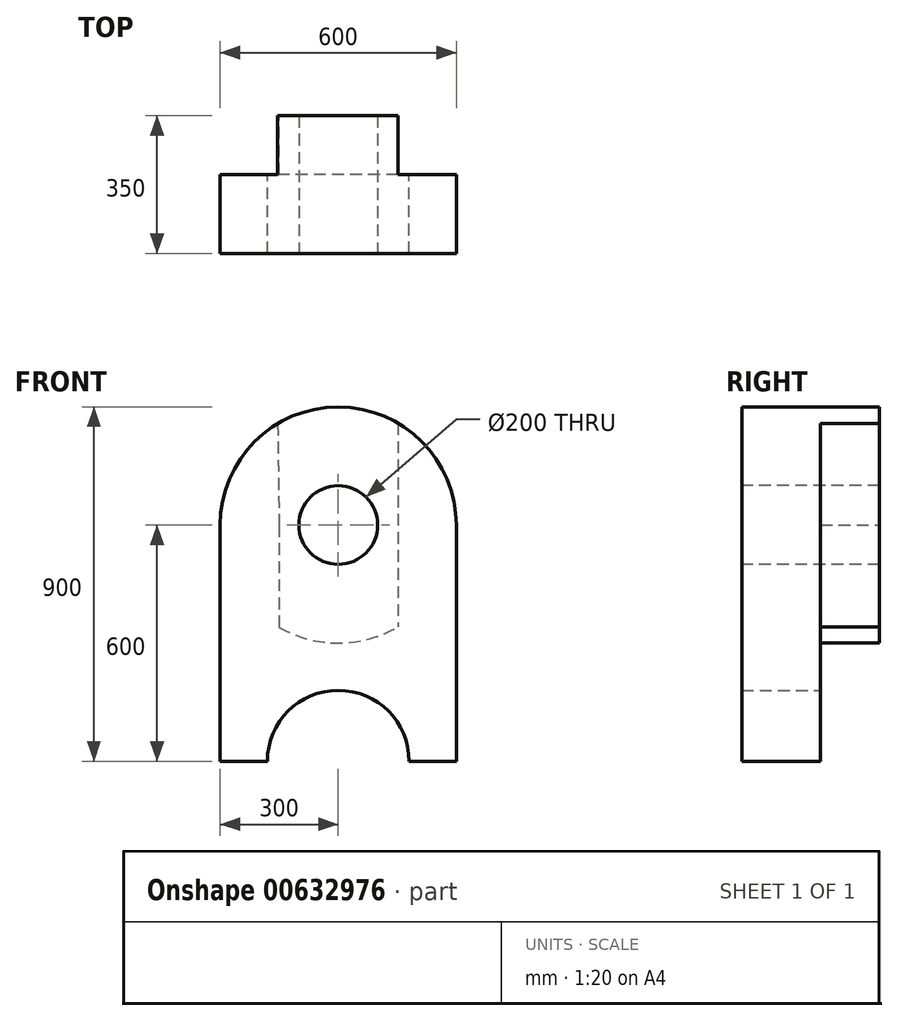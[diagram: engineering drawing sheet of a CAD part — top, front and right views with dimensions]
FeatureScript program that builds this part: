
annotation { "Feature Type Name" : "Feature", "Feature Type Description" : "" }
export const myFeature = defineFeature(function(context is Context, id is Id, definition is map)
    precondition{}
    {
        {
            var Q0;
            Q0=qCreatedBy(makeId("Front.planeOp"),FACE);
            var sketch = newSketch(context, id + "F0", { "sketchPlane" : qUnion([Q0])});
            skLineSegment(sketch, "E0.bottom", {"start": v(300, 300) * mm, "end": v(-300, 300) * mm});
            skLineSegment(sketch, "E0.top", {"start": v(300, -300) * mm, "end": v(-300, -300) * mm});
            skLineSegment(sketch, "E0.left", {"start": v(300, 300) * mm, "end": v(300, -300) * mm});
            skLineSegment(sketch, "E0.right", {"start": v(-300, 300) * mm, "end": v(-300, -300) * mm});
            skPoint(sketch, "E0.middle", {"position": v(0, 0) * mm});
            skArc(sketch, "E1", {"start": v(300, 300) * mm, "mid": v(0, 600) * mm, "end": v(-300, 300) * mm});
            skArc(sketch, "E2", {"start": v(180, -300) * mm, "mid": v(0, -120) * mm, "end": v(-180, -300) * mm});
            skSolve(sketch);
        }
        {
            var Q0;
            {var subQ0=sQuery(id+"F0.wireOp",EDGE,"E2");Q0=makeQuery(id+"F0.imprint","IMPRINT",FACE,{"disambiguationData":[TD([[makeQuery(id+"F0.imprint","IMPRINT",EDGE,{"derivedFrom":subQ0}),1.0]])]});}
            var sketch = newSketch(context, id + "F1", { "sketchPlane" : qUnion([Q0])});
            skSolve(sketch);
        }
        {
            var Q0;
            Q0=makeQuery(id+"F0.imprint","IMPRINT",FACE,{"disambiguationData":[TD([[makeQuery(id+"F0.imprint","IMPRINT",EDGE,{"derivedFrom":sQuery(id+"F0.wireOp",EDGE,"E0.bottom")}),1.0]])]});
            var Q1;
            Q1=makeQuery(id+"F0.imprint","IMPRINT",FACE,{"disambiguationData":[TD([[makeQuery(id+"F0.imprint","IMPRINT",EDGE,{"derivedFrom":sQuery(id+"F0.wireOp",EDGE,"E0.bottom")}),-1.0]])]});
            extrude(context, id + "F2", {"entities" : qUnion([Q0, Q1]), "depth" : 350 * mm, "offsetDistance" : 25 * mm});
        }
        {
            var Q0;
            {var subQ0=sQuery(id+"F0.wireOp",EDGE,"E2");Q0=makeQuery(id+"F1.imprint","IMPRINT",FACE,{"disambiguationData":[TD([[makeQuery(id+"F1.imprint","IMPRINT",EDGE,{"derivedFrom":makeQuery(id+"F0.imprint","IMPRINT",EDGE,{"derivedFrom":subQ0})}),1.0]])]});}
            extrude(context, id + "F3", {"entities" : qUnion([Q0]), "operationType" : NewBodyOperationType.REMOVE, "oppositeDirection" : true, "depth" : 25 * mm, "offsetDistance" : 25 * mm});
        }
        {
            var Q0;
            Q0=makeQuery(id+"F2.opExtrude","CAP_FACE",FACE,{"disambiguationData":[OSD([sQuery(id+"F0.wireOp",EDGE,"E0.top"),sQuery(id+"F0.wireOp",EDGE,"E0.left"),sQuery(id+"F0.wireOp",EDGE,"E0.right"),sQuery(id+"F0.wireOp",EDGE,"E1"),sQuery(id+"F0.wireOp",EDGE,"E2")])],"isStart":false});
            var sketch = newSketch(context, id + "F4", { "sketchPlane" : qUnion([Q0])});
            skCircle(sketch, "E3", {"center": v(0, 300) * mm, "radius": 100 * mm});
            skSolve(sketch);
        }
        {
            var Q0;
            Q0 = qSketchRegion(id + "F4", true);
            extrude(context, id + "F5", {"entities" : qUnion([Q0]), "operationType" : NewBodyOperationType.REMOVE, "endBound" : BoundingType.THROUGH_ALL, "oppositeDirection" : true, "depth" : 25 * mm, "offsetDistance" : 25 * mm});
        }
        {
            var Q0;
            Q0=makeQuery(id+"F2.opExtrude","CAP_FACE",FACE,{"disambiguationData":[OSD([sQuery(id+"F0.wireOp",EDGE,"E0.top"),sQuery(id+"F0.wireOp",EDGE,"E0.left"),sQuery(id+"F0.wireOp",EDGE,"E0.right"),sQuery(id+"F0.wireOp",EDGE,"E1"),sQuery(id+"F0.wireOp",EDGE,"E2")])],"isStart":true});
            var sketch = newSketch(context, id + "F6", { "sketchPlane" : qUnion([Q0])});
            skArc(sketch, "E4", {"start": v(-152.15, 41.44) * mm, "mid": v(-1.24, 0) * mm, "end": v(150, 40.2) * mm});
            skPoint(sketch, "E5", {"position": v(-300, 300) * mm});
            skPoint(sketch, "E6", {"position": v(-150, 300) * mm});
            skPoint(sketch, "E7", {"position": v(300, 300) * mm});
            skPoint(sketch, "E8", {"position": v(150, 300) * mm});
            skLineSegment(sketch, "E9", {"start": v(-152.15, 558.56) * mm, "end": v(-152.15, 41.44) * mm});
            skLineSegment(sketch, "E10", {"start": v(153.71, 557.63) * mm, "end": v(150, 300) * mm});
            skLineSegment(sketch, "E11", {"start": v(150, 300) * mm, "end": v(150, 40.2) * mm});
            skArc(sketch, "E12.trimOffspring", {"start": v(153.71, 557.63) * mm, "mid": v(0.9, 600) * mm, "end": v(-152.15, 558.56) * mm});
            skSolve(sketch);
        }
        {
            var Q0;
            Q0=makeQuery(id+"F6.imprint","IMPRINT",FACE,{"disambiguationData":[TD([[makeQuery(id+"F6.imprint","IMPRINT",EDGE,{"derivedFrom":sQuery(id+"F6.wireOp",EDGE,"E4")}),-1.0]])]});
            extrude(context, id + "F7", {"entities" : qUnion([Q0]), "operationType" : NewBodyOperationType.REMOVE, "oppositeDirection" : true, "depth" : 150 * mm, "offsetDistance" : 25 * mm});
        }
    });
